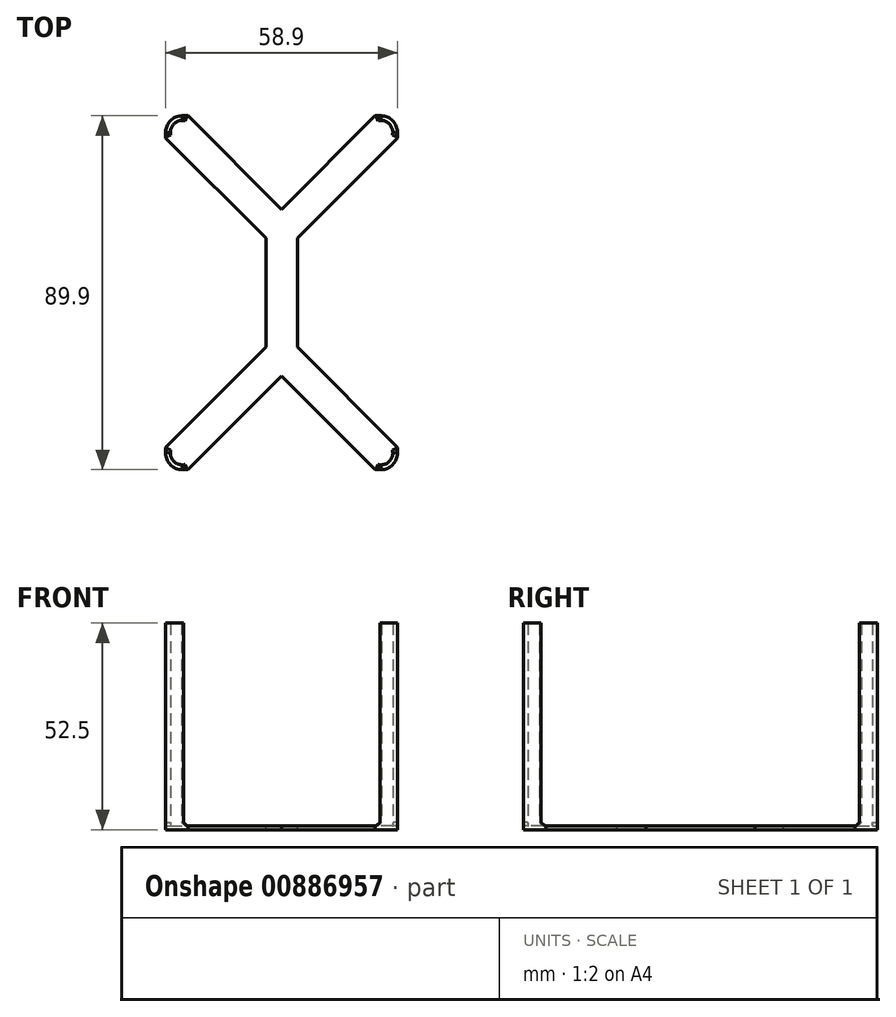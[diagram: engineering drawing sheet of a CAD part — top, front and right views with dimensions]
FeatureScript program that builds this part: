
annotation { "Feature Type Name" : "Feature", "Feature Type Description" : "" }
export const myFeature = defineFeature(function(context is Context, id is Id, definition is map)
    precondition{}
    {
        {
            assignVariable(context, id + "F0", {"name" : "DeckHeight", "anyValue" : 50.5});
        }
        {
            var Q0;
            Q0=qCreatedBy(makeId("Top.planeOp"),FACE);
            var sketch = newSketch(context, id + "F1", { "sketchPlane" : qUnion([Q0])});
            skLineSegment(sketch, "E0.bottom", {"start": v(28.25, -43.75) * mm, "end": v(-28.25, -43.75) * mm, "construction": true});
            skLineSegment(sketch, "E0.top", {"start": v(28.25, 43.75) * mm, "end": v(-28.25, 43.75) * mm, "construction": true});
            skLineSegment(sketch, "E0.left", {"start": v(28.25, -43.75) * mm, "end": v(28.25, 43.75) * mm, "construction": true});
            skLineSegment(sketch, "E0.right", {"start": v(-28.25, -43.75) * mm, "end": v(-28.25, 43.75) * mm, "construction": true});
            skPoint(sketch, "E0.middle", {"position": v(0, 0) * mm});
            skLineSegment(sketch, "E1", {"start": v(-4, 0) * mm, "end": v(-4, -13.84) * mm});
            skLineSegment(sketch, "E2", {"start": v(-4, -13.84) * mm, "end": v(-29.45, -39.3) * mm});
            skLineSegment(sketch, "E3", {"start": v(-29.45, -39.3) * mm, "end": v(-29.45, -40.75) * mm});
            skLineSegment(sketch, "E4", {"start": v(0, -21.16) * mm, "end": v(-23.8, -44.95) * mm});
            skLineSegment(sketch, "E5", {"start": v(-23.8, -44.95) * mm, "end": v(-25.25, -44.95) * mm});
            skArc(sketch, "E6", {"start": v(-28.25, -40.75) * mm, "mid": v(-27.37, -42.87) * mm, "end": v(-25.25, -43.75) * mm});
            skLineSegment(sketch, "E7", {"start": v(-28.25, -40.75) * mm, "end": v(-28.25, -38.1) * mm});
            skLineSegment(sketch, "E8", {"start": v(-25.25, -43.75) * mm, "end": v(-22.6, -43.75) * mm});
            skArc(sketch, "E9", {"start": v(-25.25, -44.95) * mm, "mid": v(-28.22, -43.72) * mm, "end": v(-29.45, -40.75) * mm});
            skLineSegment(sketch, "E10", {"start": v(0, 0) * mm, "end": v(-4, 0) * mm});
            skLineSegment(sketch, "E11", {"start": v(0, 0) * mm, "end": v(0, -21.16) * mm});
            skSolve(sketch);
        }
        {
            var Q0;
            {var subQ4=sQuery(id+"F1.wireOp",EDGE,"E1");Q0=makeQuery(id+"F1.imprint","IMPRINT",FACE,{"disambiguationData":[TD([[makeQuery(id+"F1.imprint","IMPRINT",EDGE,{"derivedFrom":subQ4}),1.0]])]});}
            var Q1;
            {var subQ3=sQuery(id+"F1.wireOp",EDGE,"E3");Q1=makeQuery(id+"F1.imprint","IMPRINT",FACE,{"disambiguationData":[TD([[makeQuery(id+"F1.imprint","IMPRINT",EDGE,{"derivedFrom":subQ3}),1.0]])]});}
            extrude(context, id + "F2", {"entities" : qUnion([Q0, Q1]), "oppositeDirection" : true, "depth" : 1 * mm, "offsetDistance" : 25 * mm});
        }
        {
            var Q0;
            {var subQ3=sQuery(id+"F1.wireOp",EDGE,"E3");Q0=makeQuery(id+"F1.imprint","IMPRINT",FACE,{"disambiguationData":[TD([[makeQuery(id+"F1.imprint","IMPRINT",EDGE,{"derivedFrom":subQ3}),1.0]])]});}
            extrude(context, id + "F3", {"entities" : qUnion([Q0]), "operationType" : NewBodyOperationType.ADD, "depth" : (getVariable(context, 'DeckHeight')) * mm, "offsetDistance" : 25 * mm});
        }
        {
            var Q0;
            Q0=makeQuery(id+"F3.opExtrude","SWEPT_EDGE",EDGE,{"disambiguationData":[OSD([sQuery(id+"F1.wireOp",EDGE,"E2"),sQuery(id+"F1.wireOp",EDGE,"E7")])]});
            var Q1;
            Q1=makeQuery(id+"F3.opExtrude","SWEPT_EDGE",EDGE,{"disambiguationData":[OSD([sQuery(id+"F1.wireOp",EDGE,"E4"),sQuery(id+"F1.wireOp",EDGE,"E8")])]});
            chamfer(context, id + "F4", {"entities" : qUnion([Q0, Q1]), "width" : 1.2 * mm, "tangentPropagation" : true});
        }
        {
            var Q0;
            {var subQ0=sQuery(id+"F1.wireOp",EDGE,"E4");Q0=makeQuery(id+"F4.opChamfer","BLEND_EDGE",EDGE,{"blendedFrom":[makeQuery(id+"F3.opExtrude","SWEPT_EDGE",EDGE,{"disambiguationData":[OSD([subQ0,sQuery(id+"F1.wireOp",EDGE,"E8")])]}),makeQuery(id+"F2.opExtrude","CAP_FACE",FACE,{"disambiguationData":[OSD([sQuery(id+"F1.wireOp",EDGE,"E1"),sQuery(id+"F1.wireOp",EDGE,"E2"),sQuery(id+"F1.wireOp",EDGE,"E3"),subQ0,sQuery(id+"F1.wireOp",EDGE,"E5"),sQuery(id+"F1.wireOp",EDGE,"E9"),sQuery(id+"F1.wireOp",EDGE,"E10"),sQuery(id+"F1.wireOp",EDGE,"E11")])],"isStart":true})],"blendedInto":[makeQuery(id+"F2.opExtrude","CAP_FACE",FACE,{"disambiguationData":[OSD([sQuery(id+"F1.wireOp",EDGE,"E1"),sQuery(id+"F1.wireOp",EDGE,"E2"),sQuery(id+"F1.wireOp",EDGE,"E3"),subQ0,sQuery(id+"F1.wireOp",EDGE,"E5"),sQuery(id+"F1.wireOp",EDGE,"E9"),sQuery(id+"F1.wireOp",EDGE,"E10"),sQuery(id+"F1.wireOp",EDGE,"E11")])],"isStart":true})]});}
            var Q1;
            {var subQ0=sQuery(id+"F1.wireOp",EDGE,"E2");Q1=makeQuery(id+"F4.opChamfer","BLEND_EDGE",EDGE,{"blendedFrom":[makeQuery(id+"F3.opExtrude","SWEPT_EDGE",EDGE,{"disambiguationData":[OSD([subQ0,sQuery(id+"F1.wireOp",EDGE,"E7")])]}),makeQuery(id+"F2.opExtrude","CAP_FACE",FACE,{"disambiguationData":[OSD([sQuery(id+"F1.wireOp",EDGE,"E1"),subQ0,sQuery(id+"F1.wireOp",EDGE,"E3"),sQuery(id+"F1.wireOp",EDGE,"E4"),sQuery(id+"F1.wireOp",EDGE,"E5"),sQuery(id+"F1.wireOp",EDGE,"E9"),sQuery(id+"F1.wireOp",EDGE,"E10"),sQuery(id+"F1.wireOp",EDGE,"E11")])],"isStart":true})],"blendedInto":[makeQuery(id+"F2.opExtrude","CAP_FACE",FACE,{"disambiguationData":[OSD([sQuery(id+"F1.wireOp",EDGE,"E1"),subQ0,sQuery(id+"F1.wireOp",EDGE,"E3"),sQuery(id+"F1.wireOp",EDGE,"E4"),sQuery(id+"F1.wireOp",EDGE,"E5"),sQuery(id+"F1.wireOp",EDGE,"E9"),sQuery(id+"F1.wireOp",EDGE,"E10"),sQuery(id+"F1.wireOp",EDGE,"E11")])],"isStart":true})]});}
            chamfer(context, id + "F5", {"entities" : qUnion([Q0, Q1]), "width" : 0.9 * mm, "tangentPropagation" : true});
        }
        {
            var Q0;
            Q0=makeQuery(id+"F3.opExtrude","CAP_FACE",FACE,{"disambiguationData":[OSD([sQuery(id+"F1.wireOp",EDGE,"E2"),sQuery(id+"F1.wireOp",EDGE,"E3"),sQuery(id+"F1.wireOp",EDGE,"E4"),sQuery(id+"F1.wireOp",EDGE,"E5"),sQuery(id+"F1.wireOp",EDGE,"E6"),sQuery(id+"F1.wireOp",EDGE,"E7"),sQuery(id+"F1.wireOp",EDGE,"E8"),sQuery(id+"F1.wireOp",EDGE,"E9")])],"isStart":false});
            var sketch = newSketch(context, id + "F6", { "sketchPlane" : qUnion([Q0])});
            skLineSegment(sketch, "E12", {"start": v(-23.8, -43.75) * mm, "end": v(-28.25, -39.3) * mm});
            skSolve(sketch);
        }
        {
            var Q0;
            Q0=makeQuery(id+"F6.imprint","IMPRINT",FACE,{"disambiguationData":[TD([[makeQuery(id+"F6.imprint","IMPRINT",EDGE,{"derivedFrom":sQuery(id+"F6.wireOp",EDGE,"E12")}),1.0]])]});
            var Q1;
            {var subQ3=sQuery(id+"F1.wireOp",EDGE,"E3");Q1=makeQuery(id+"F6.imprint","IMPRINT",FACE,{"disambiguationData":[TD([[makeQuery(id+"F6.imprint","IMPRINT",EDGE,{"derivedFrom":makeQuery(id+"F3.opExtrude","CAP_EDGE",EDGE,{"disambiguationData":[OSD([subQ3])],"isStart":false})}),1.0]])]});}
            extrude(context, id + "F7", {"entities" : qUnion([Q0, Q1]), "operationType" : NewBodyOperationType.ADD, "depth" : 1 * mm, "offsetDistance" : 25 * mm});
        }
        {
            var Q0;
            Q0=makeQuery(id+"F2.opExtrude","SWEPT_BODY",BODY,{"disambiguationData":[OSD([sQuery(id+"F1.wireOp",EDGE,"E1"),sQuery(id+"F1.wireOp",EDGE,"E2"),sQuery(id+"F1.wireOp",EDGE,"E3"),sQuery(id+"F1.wireOp",EDGE,"E4"),sQuery(id+"F1.wireOp",EDGE,"E5"),sQuery(id+"F1.wireOp",EDGE,"E9"),sQuery(id+"F1.wireOp",EDGE,"E10"),sQuery(id+"F1.wireOp",EDGE,"E11")])]});
            var Q1;
            Q1=makeQuery(id+"F2.opExtrude","SWEPT_FACE",FACE,{"disambiguationData":[OSD([sQuery(id+"F1.wireOp",EDGE,"E11")])]});
            mirror(context, id + "F8", {"operationType" : NewBodyOperationType.ADD, "entities" : qUnion([Q0]), "mirrorPlane" : qUnion([Q1])});
        }
        {
            var Q0;
            Q0=makeQuery(id+"F2.opExtrude","SWEPT_BODY",BODY,{"disambiguationData":[OSD([sQuery(id+"F1.wireOp",EDGE,"E1"),sQuery(id+"F1.wireOp",EDGE,"E2"),sQuery(id+"F1.wireOp",EDGE,"E3"),sQuery(id+"F1.wireOp",EDGE,"E4"),sQuery(id+"F1.wireOp",EDGE,"E5"),sQuery(id+"F1.wireOp",EDGE,"E9"),sQuery(id+"F1.wireOp",EDGE,"E10"),sQuery(id+"F1.wireOp",EDGE,"E11")])]});
            var Q1;
            {var subQ0=makeQuery(id+"F2.opExtrude","SWEPT_FACE",FACE,{"disambiguationData":[OSD([sQuery(id+"F1.wireOp",EDGE,"E10")])]});Q1=makeQuery(id+"F8.boolean.opBoolean","MERGE",FACE,{"derivedFrom":[subQ0,makeQuery(id+"F8.opPattern","COPY",FACE,{"derivedFrom":subQ0,"instanceName":"1"})]});}
            mirror(context, id + "F9", {"operationType" : NewBodyOperationType.ADD, "entities" : qUnion([Q0]), "mirrorPlane" : qUnion([Q1])});
        }
    });
